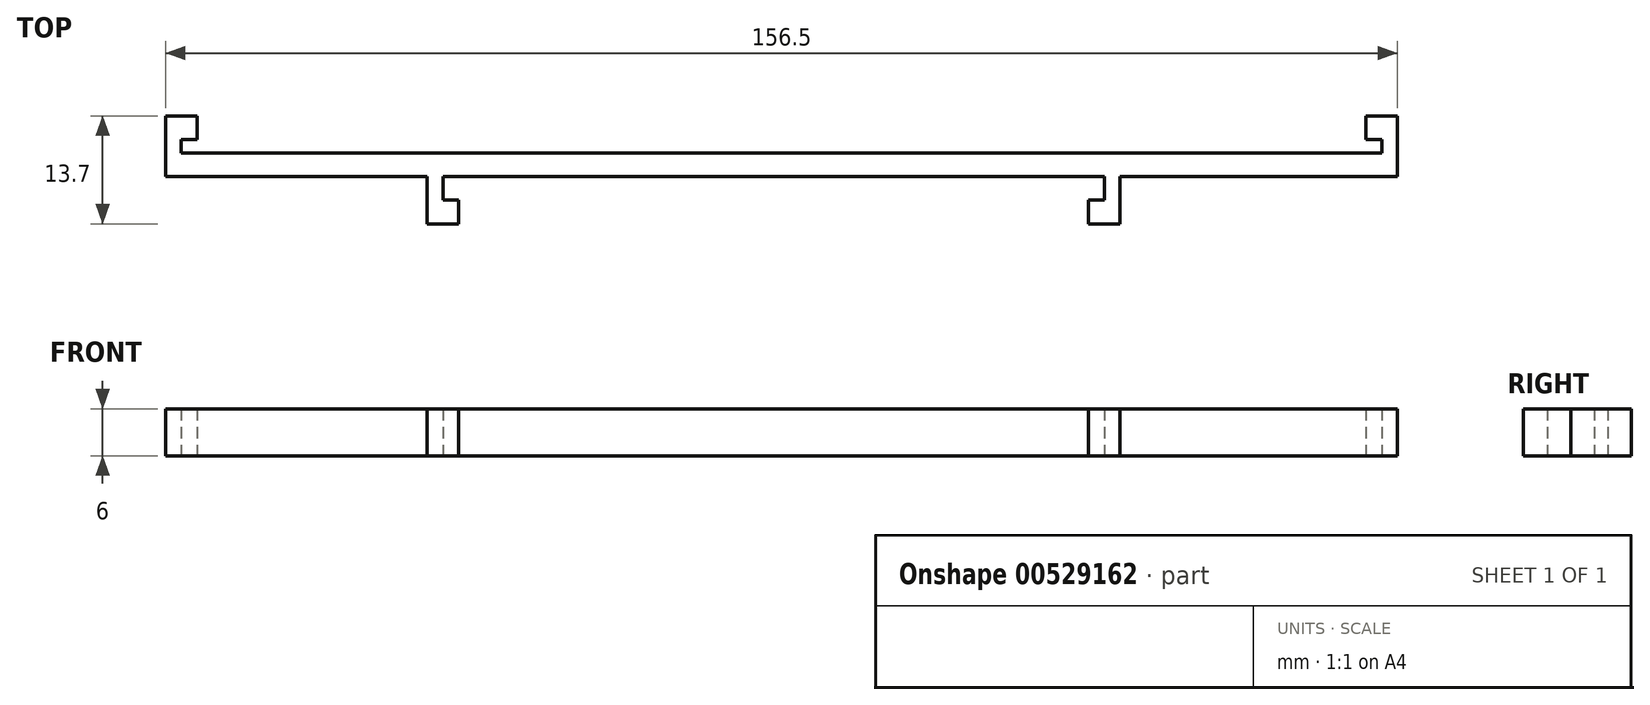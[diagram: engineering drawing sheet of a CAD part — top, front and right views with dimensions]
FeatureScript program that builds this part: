
annotation { "Feature Type Name" : "Feature", "Feature Type Description" : "" }
export const myFeature = defineFeature(function(context is Context, id is Id, definition is map)
    precondition{}
    {
        {
            var Q0;
            Q0=qCreatedBy(makeId("Top.planeOp"),FACE);
            var sketch = newSketch(context, id + "F0", { "sketchPlane" : qUnion([Q0])});
            skLineSegment(sketch, "E0", {"start": v(-88.85, 9.42) * mm, "end": v(81.15, 9.42) * mm, "construction": true});
            skLineSegment(sketch, "E1", {"start": v(-88.85, -7.28) * mm, "end": v(81.15, -7.28) * mm, "construction": true});
            skLineSegment(sketch, "E2", {"start": v(-88.85, 1.72) * mm, "end": v(81.15, 1.72) * mm, "construction": true});
            skLineSegment(sketch, "E3", {"start": v(-77.3, 17.34) * mm, "end": v(-77.3, -16) * mm, "construction": true});
            skLineSegment(sketch, "E4", {"start": v(79.2, 16.82) * mm, "end": v(79.2, -14.78) * mm, "construction": true});
            skLineSegment(sketch, "E5", {"start": v(-75.3, 17.22) * mm, "end": v(-75.3, -16) * mm, "construction": true});
            skLineSegment(sketch, "E6", {"start": v(77.2, 16.82) * mm, "end": v(77.2, -14.78) * mm, "construction": true});
            skLineSegment(sketch, "E7", {"start": v(-88.85, 6.42) * mm, "end": v(81.15, 6.42) * mm, "construction": true});
            skLineSegment(sketch, "E8", {"start": v(-88.85, 4.72) * mm, "end": v(81.15, 4.72) * mm, "construction": true});
            skLineSegment(sketch, "E9", {"start": v(-73.3, 17.22) * mm, "end": v(-73.3, -16) * mm, "construction": true});
            skLineSegment(sketch, "E10", {"start": v(75.2, 16.82) * mm, "end": v(75.2, -14.78) * mm, "construction": true});
            skLineSegment(sketch, "E11", {"start": v(-73.3, 9.42) * mm, "end": v(-77.3, 9.42) * mm});
            skLineSegment(sketch, "E12", {"start": v(-77.3, 9.42) * mm, "end": v(-77.3, 1.72) * mm});
            skLineSegment(sketch, "E13", {"start": v(-77.3, 1.72) * mm, "end": v(-44.05, 1.72) * mm});
            skLineSegment(sketch, "E14", {"start": v(79.2, 1.72) * mm, "end": v(79.2, 9.42) * mm});
            skLineSegment(sketch, "E15", {"start": v(79.2, 9.42) * mm, "end": v(75.2, 9.42) * mm});
            skLineSegment(sketch, "E16", {"start": v(75.2, 9.42) * mm, "end": v(75.2, 6.42) * mm});
            skLineSegment(sketch, "E17", {"start": v(75.2, 6.42) * mm, "end": v(77.2, 6.42) * mm});
            skLineSegment(sketch, "E18", {"start": v(77.2, 6.42) * mm, "end": v(77.2, 4.72) * mm});
            skLineSegment(sketch, "E19", {"start": v(77.2, 4.72) * mm, "end": v(-75.3, 4.72) * mm});
            skLineSegment(sketch, "E20", {"start": v(-75.3, 4.72) * mm, "end": v(-75.3, 6.42) * mm});
            skLineSegment(sketch, "E21", {"start": v(-75.3, 6.42) * mm, "end": v(-73.3, 6.42) * mm});
            skLineSegment(sketch, "E22", {"start": v(-73.3, 6.42) * mm, "end": v(-73.3, 9.42) * mm});
            skLineSegment(sketch, "E23", {"start": v(-0.05, 22.09) * mm, "end": v(-0.05, -13.48) * mm, "construction": true});
            skLineSegment(sketch, "E24", {"start": v(-49.35, -4.28) * mm, "end": v(-40.05, -4.28) * mm, "construction": true});
            skLineSegment(sketch, "E25", {"start": v(-44.05, 13.03) * mm, "end": v(-44.05, -15.94) * mm, "construction": true});
            skLineSegment(sketch, "E26.MirrorCS", {"start": v(43.95, 13.03) * mm, "end": v(43.95, -15.94) * mm, "construction": true});
            skLineSegment(sketch, "E27", {"start": v(-55.61, -1.28) * mm, "end": v(-42.05, -1.28) * mm, "construction": true});
            skLineSegment(sketch, "E28", {"start": v(-40.05, 13.03) * mm, "end": v(-40.05, -15.94) * mm, "construction": true});
            skLineSegment(sketch, "E29.MirrorCS", {"start": v(39.95, 13.03) * mm, "end": v(39.95, -15.94) * mm, "construction": true});
            skLineSegment(sketch, "E30", {"start": v(-44.05, 1.72) * mm, "end": v(-44.05, -4.28) * mm});
            skLineSegment(sketch, "E31", {"start": v(-44.05, -4.28) * mm, "end": v(-40.05, -4.28) * mm});
            skLineSegment(sketch, "E32", {"start": v(-40.05, -1.28) * mm, "end": v(-42.05, -1.28) * mm});
            skLineSegment(sketch, "E33", {"start": v(43.95, 1.72) * mm, "end": v(43.95, -4.28) * mm});
            skLineSegment(sketch, "E34", {"start": v(43.95, -4.28) * mm, "end": v(39.95, -4.28) * mm});
            skLineSegment(sketch, "E35", {"start": v(39.95, -1.28) * mm, "end": v(41.95, -1.28) * mm});
            skLineSegment(sketch, "E36.trimOffspring", {"start": v(-42.05, 1.72) * mm, "end": v(41.95, 1.72) * mm});
            skLineSegment(sketch, "E37.trimOffspring", {"start": v(43.95, 1.72) * mm, "end": v(79.2, 1.72) * mm});
            skLineSegment(sketch, "E38", {"start": v(-42.05, 13.17) * mm, "end": v(-42.05, -23.6) * mm, "construction": true});
            skLineSegment(sketch, "E39", {"start": v(-42.05, 1.72) * mm, "end": v(-42.05, 1.72) * mm});
            skLineSegment(sketch, "E40", {"start": v(-42.05, 1.72) * mm, "end": v(-42.05, -1.28) * mm});
            skLineSegment(sketch, "E41", {"start": v(-42.05, -1.28) * mm, "end": v(-42.05, -1.28) * mm});
            skLineSegment(sketch, "E42.MirrorCS", {"start": v(41.95, 13.17) * mm, "end": v(41.95, -23.6) * mm, "construction": true});
            skLineSegment(sketch, "E43", {"start": v(41.95, -1.28) * mm, "end": v(41.95, -1.28) * mm});
            skLineSegment(sketch, "E44", {"start": v(41.95, -1.28) * mm, "end": v(41.95, 1.72) * mm});
            skLineSegment(sketch, "E45", {"start": v(41.95, 1.72) * mm, "end": v(41.95, 1.72) * mm});
            skLineSegment(sketch, "E46", {"start": v(-40.05, -1.28) * mm, "end": v(-40.05, -4.28) * mm});
            skLineSegment(sketch, "E47.trimOffspring", {"start": v(-38.05, -1.28) * mm, "end": v(37.95, -1.28) * mm, "construction": true});
            skLineSegment(sketch, "E48.trimOffspring", {"start": v(-38.05, -4.28) * mm, "end": v(37.95, -4.28) * mm, "construction": true});
            skLineSegment(sketch, "E49", {"start": v(39.95, -1.28) * mm, "end": v(39.95, -4.28) * mm});
            skLineSegment(sketch, "E50.trimOffspring", {"start": v(39.95, -1.28) * mm, "end": v(50.64, -1.28) * mm, "construction": true});
            skLineSegment(sketch, "E51.trimOffspring", {"start": v(39.95, -4.28) * mm, "end": v(48.49, -4.28) * mm, "construction": true});
            skSolve(sketch);
        }
        {
            var Q0;
            Q0=qSketchRegion(id+"F0",true);
            extrude(context, id + "F1", {"entities" : qUnion([Q0]), "depth" : 6 * mm, "offsetDistance" : 25 * mm});
        }
    });
